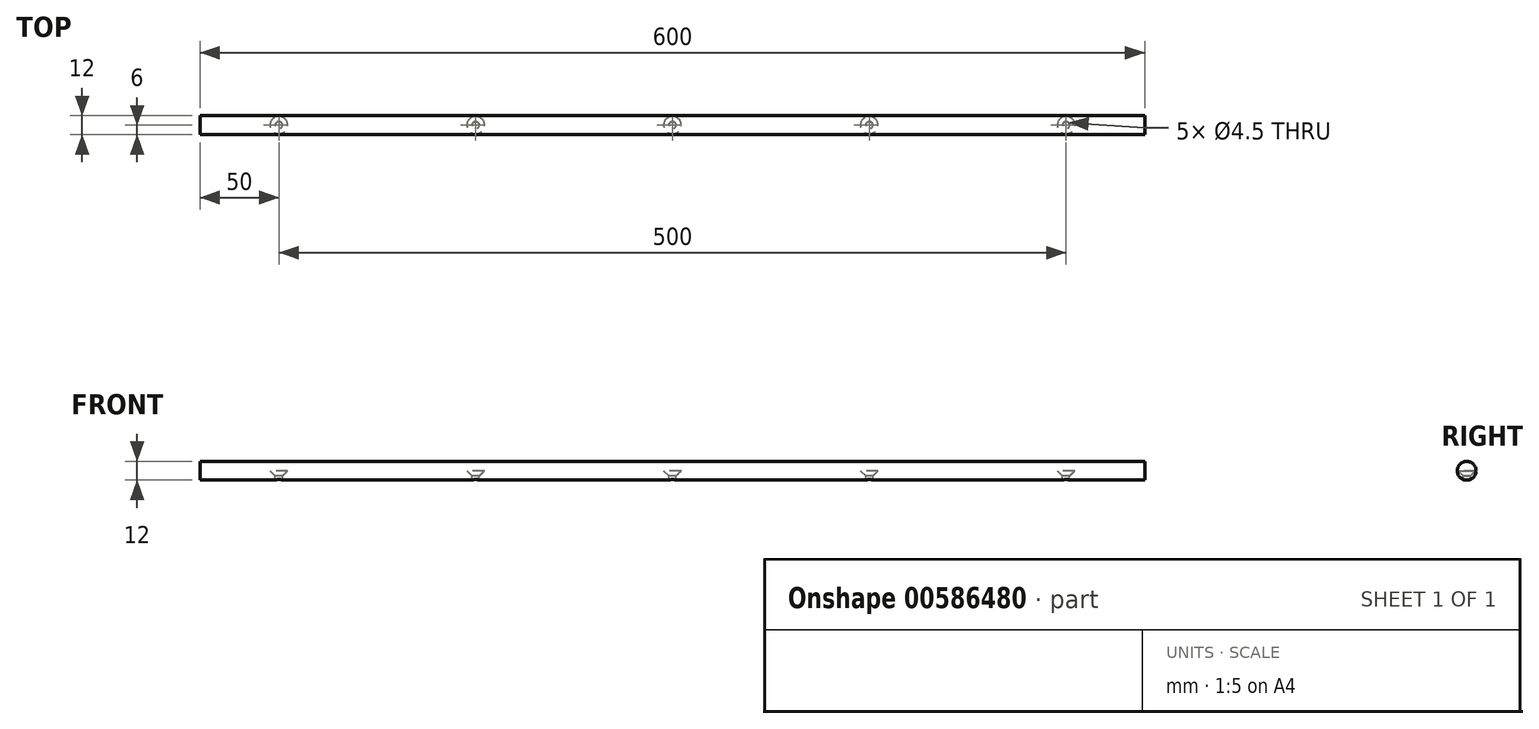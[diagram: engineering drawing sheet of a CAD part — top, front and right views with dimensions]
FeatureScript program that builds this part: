
annotation { "Feature Type Name" : "Feature", "Feature Type Description" : "" }
export const myFeature = defineFeature(function(context is Context, id is Id, definition is map)
    precondition{}
    {
        {
            var Q0;
            Q0=qCreatedBy(makeId("Right.planeOp"),FACE);
            var sketch = newSketch(context, id + "F0", { "sketchPlane" : qUnion([Q0])});
            skCircle(sketch, "E0", {"center": v(0, 0) * mm, "radius": 6 * mm});
            skLineSegment(sketch, "E1", {"start": v(0, 6) * mm, "end": v(15.02, 6) * mm});
            skSolve(sketch);
        }
        {
            var Q0;
            Q0=makeQuery(id+"F0.imprint","IMPRINT",FACE,{"disambiguationData":[TD([[makeQuery(id+"F0.imprint","IMPRINT",EDGE,{"derivedFrom":sQuery(id+"F0.wireOp",EDGE,"E0")}),1.0]])]});
            extrude(context, id + "F1", {"entities" : qUnion([Q0]), "depth" : 600 * mm, "offsetDistance" : 25 * mm});
        }
        {
            var Q0;
            Q0=qCreatedBy(makeId("Top.planeOp"),FACE);
            var sketch = newSketch(context, id + "F2", { "sketchPlane" : qUnion([Q0])});
            skCircle(sketch, "E2", {"center": v(50, 0) * mm, "radius": 2.78 * mm});
            skCircle(sketch, "E3", {"center": v(175, 0) * mm, "radius": 3.72 * mm});
            skCircle(sketch, "E4", {"center": v(300, 0) * mm, "radius": 2.38 * mm});
            skCircle(sketch, "E5", {"center": v(425, 0) * mm, "radius": 2.13 * mm});
            skCircle(sketch, "E6", {"center": v(550, 0) * mm, "radius": 3.1 * mm});
            skLineSegment(sketch, "E7", {"start": v(0, 0) * mm, "end": v(-10.1, 0) * mm});
            skSolve(sketch);
        }
        {
            var Q0;
            Q0=sQuery(id+"F2.wireOp",VERTEX,"E2.center");
            var Q1;
            Q1=sQuery(id+"F2.wireOp",VERTEX,"E3.center");
            var Q2;
            Q2=sQuery(id+"F2.wireOp",VERTEX,"E4.center");
            var Q3;
            Q3=sQuery(id+"F2.wireOp",VERTEX,"E6.center");
            var Q4;
            Q4=sQuery(id+"F2.wireOp",VERTEX,"E5.center");
            var Q5;
            Q5=makeQuery(id+"F1.opExtrude","SWEPT_BODY",BODY,{"disambiguationData":[OSD([sQuery(id+"F0.wireOp",EDGE,"E0")])]});
            hole(context, id + "F3", {"style" : HoleStyle.C_SINK, "endStyle" : HoleEndStyle.BLIND, "standardTappedOrClearance" : lookupTablePath({ "standard" : "ISO", "engagement" : "75%", "pitch" : "0.5 mm", "size" : "M5", "type" : "Tapped" }), "standardBlindInLast" : lookupTablePath({ "standard" : "ISO", "engagement" : "75%", "pitch" : "0.5 mm", "size" : "M5", "type" : "Tapped" }), "holeDiameter" : 4.5 * mm, "cSinkDiameter" : 11.2 * mm, "cSinkAngle" : 90 * degree, "majorDiameter" : 5 * mm, "showTappedDepth" : true, "holeDepth" : 9.1 * mm, "isTappedThrough" : true, "tappedDepth" : 7.6 * mm, "tapClearance" : 3, "locations" : qUnion([Q0, Q1, Q2, Q3, Q4]), "scope" : qUnion([Q5])});
        }
    });
